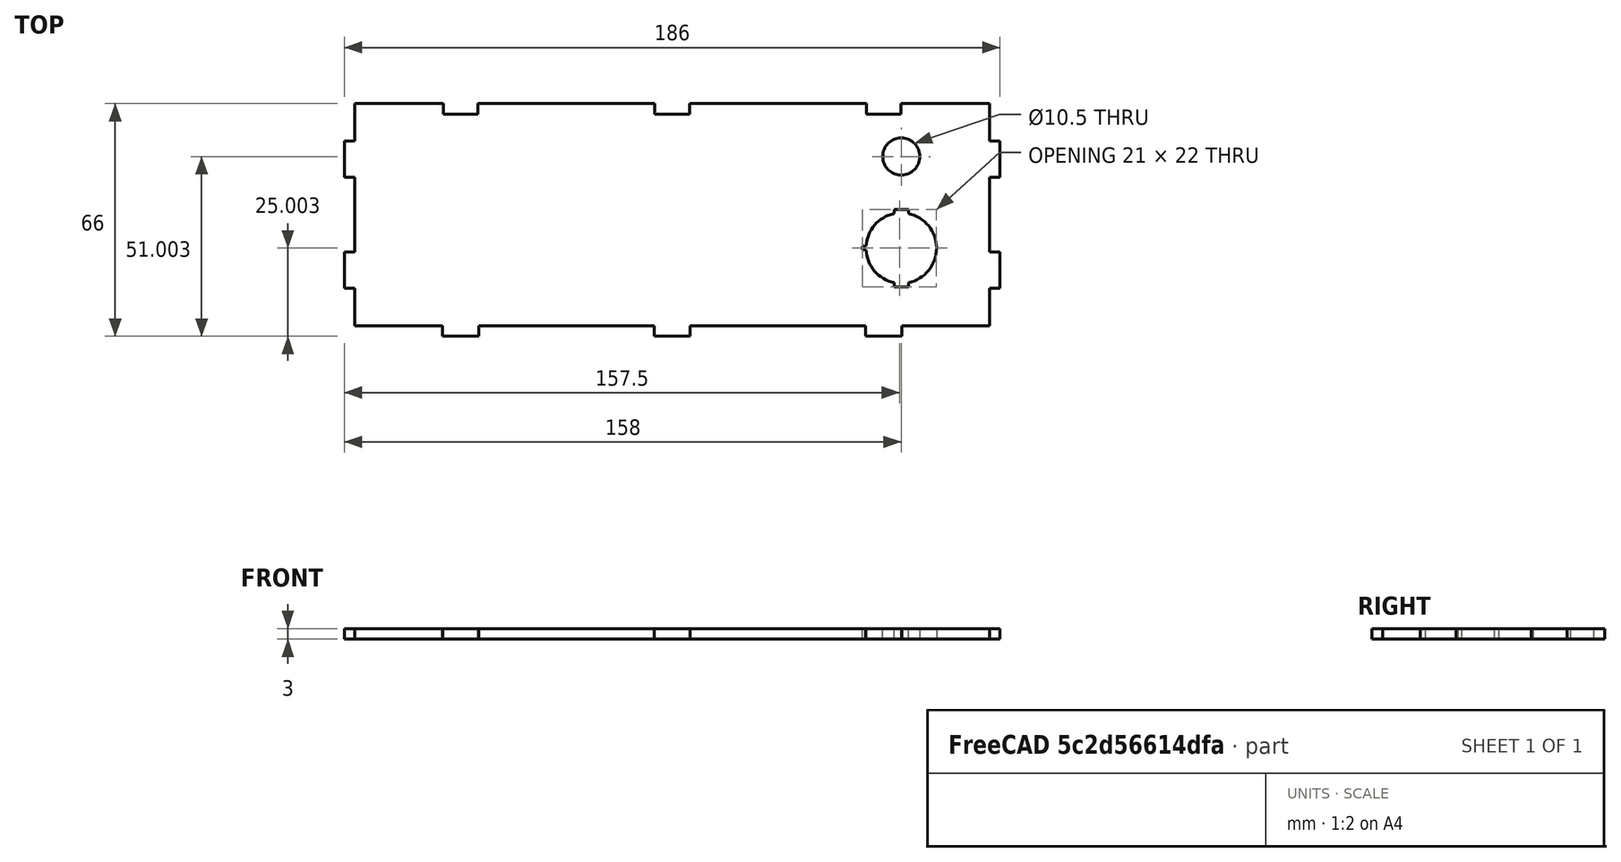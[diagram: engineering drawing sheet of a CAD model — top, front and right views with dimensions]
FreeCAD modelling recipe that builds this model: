
FCSTD DOCUMENT  (FreeCAD 0.21R33771 (Git))
Label: point-controller-box-v0.5.5-expand-updated
License: All rights reserved
LicenseURL: http://en.wikipedia.org/wiki/All_rights_reserved
objects: Part::Feature×7, Part::Part2DObjectPython×7, Sketcher::SketchObject×6, Part::Mirroring×1
note: 21 computed .brp shape members not serialized (recipe doc carries the construction recipe); baked Part::Feature solids carry a one-line shape summary decoded from their .brp

FEATURE [Part::Feature] test
  Placement = pos=(93,51,93) rot=(1,0,0;1.5708rad)
  shape: bbox 186 x 51 x 3 mm, 46 faces (baked)
FEATURE [Part::Feature] test001
  Placement = pos=(196,63,-60) rot=(0,1,0;1.5708rad)
  shape: bbox 63.37 x 126 x 3 mm, 38 faces (baked)
FEATURE [Part::Feature] test002
  Placement = pos=(93,206.207,88.2734) rot=(0.121054,0,0;3.02024rad)
  shape: bbox 186 x 126.9 x 3 mm, 56 faces (baked)
FEATURE [Part::Feature] test003
  Placement = pos=(196,199,123) rot=(0,1,0;1.5708rad)
  shape: bbox 63.37 x 126 x 3 mm, 38 faces (baked)
FEATURE [Part::Feature] test004
  Placement = pos=(93,338.933,-30) rot=(1,0,0;1.5708rad)
  shape: bbox 186 x 66 x 3 mm, 46 faces (baked)
FEATURE [Part::Feature] test005
  Placement = pos=(289,335.933,33) rot=(0,1,0;3.14159rad)
  shape: bbox 186 x 126 x 3 mm, 46 faces (baked)
FEATURE [Part::Feature] test006
  Placement = pos=(93,474.933,-30) rot=(1,0,0;1.5708rad)
  shape: bbox 186 x 66 x 3 mm, 59 faces (baked)
FEATURE [Part::Part2DObjectPython] Shape2DView  label="Shape2DView-Front"  # Draft 2D object (typed FeaturePython)
  AutoUpdate = true
  Base = -> test
  Clip = false
  FuseArch = false
  HiddenLines = false
  InPlace = true
  OnlySolids = false
  Projection = (0,0,1)
  ProjectionMode = 0
  SegmentLength = 0.05
  Tessellation = false
  VisibleOnly = false
FEATURE [Part::Part2DObjectPython] Shape2DView001  # Draft 2D object (typed FeaturePython)
  AutoUpdate = true
  Base = -> test001
  Clip = false
  FuseArch = false
  HiddenLines = false
  InPlace = true
  OnlySolids = false
  Projection = (0,0,1)
  ProjectionMode = 0
  SegmentLength = 0.05
  Tessellation = false
  VisibleOnly = false
FEATURE [Part::Part2DObjectPython] Shape2DView002  # Draft 2D object (typed FeaturePython)
  AutoUpdate = true
  Base = -> test002
  Clip = false
  FuseArch = false
  HiddenLines = false
  InPlace = true
  OnlySolids = false
  Projection = (0,0,1)
  ProjectionMode = 0
  SegmentLength = 0.05
  Tessellation = false
  VisibleOnly = false
FEATURE [Part::Part2DObjectPython] Shape2DView003  # Draft 2D object (typed FeaturePython)
  AutoUpdate = true
  Base = -> test003
  Clip = false
  FuseArch = false
  HiddenLines = false
  InPlace = true
  OnlySolids = false
  Projection = (0,0,1)
  ProjectionMode = 0
  SegmentLength = 0.05
  Tessellation = false
  VisibleOnly = false
FEATURE [Part::Part2DObjectPython] Shape2DView004  # Draft 2D object (typed FeaturePython)
  AutoUpdate = true
  Base = -> test004
  Clip = false
  FuseArch = false
  HiddenLines = false
  InPlace = true
  OnlySolids = false
  Projection = (0,0,1)
  ProjectionMode = 0
  SegmentLength = 0.05
  Tessellation = false
  VisibleOnly = false
FEATURE [Part::Part2DObjectPython] Shape2DView005  # Draft 2D object (typed FeaturePython)
  AutoUpdate = true
  Base = -> test005
  Clip = false
  FuseArch = false
  HiddenLines = false
  InPlace = true
  OnlySolids = false
  Projection = (0,0,1)
  ProjectionMode = 0
  SegmentLength = 0.05
  Tessellation = false
  VisibleOnly = false
FEATURE [Part::Part2DObjectPython] Shape2DView006  # Draft 2D object (typed FeaturePython)
  AutoUpdate = true
  Base = -> test006
  Clip = false
  FuseArch = false
  HiddenLines = false
  InPlace = true
  OnlySolids = false
  Projection = (0,0,1)
  ProjectionMode = 0
  SegmentLength = 0.05
  Tessellation = false
  VisibleOnly = false
FEATURE [Sketcher::SketchObject] Sketch  label="Sketch-Front"
  FullyConstrained = false
  sketch-geometry (44):
    g0: LineSegment StartX=3 StartY=51 StartZ=0 EndX=28.1 EndY=51 EndZ=0
    g1: LineSegment StartX=28.1 StartY=51 StartZ=0 EndX=28.1 EndY=47.95 EndZ=0
    g2: LineSegment StartX=3 StartY=44.1 StartZ=0 EndX=3 EndY=51 EndZ=0
    g3: LineSegment StartX=28.1 StartY=47.95 StartZ=0 EndX=37.9 EndY=47.95 EndZ=0
    g4: LineSegment StartX=37.9 StartY=51 StartZ=0 EndX=37.9 EndY=47.95 EndZ=0
    g5: LineSegment StartX=37.9 StartY=51 StartZ=0 EndX=88.1 EndY=51 EndZ=0
    g6: LineSegment StartX=88.1 StartY=51 StartZ=0 EndX=88.1 EndY=47.95 EndZ=0
    g7: LineSegment StartX=88.1 StartY=47.95 StartZ=0 EndX=97.9 EndY=47.95 EndZ=0
    g8: LineSegment StartX=97.9 StartY=51 StartZ=0 EndX=97.9 EndY=47.95 EndZ=0
    g9: LineSegment StartX=97.9 StartY=51 StartZ=0 EndX=148.1 EndY=51 EndZ=0
    g10: LineSegment StartX=148.1 StartY=51 StartZ=0 EndX=148.1 EndY=47.95 EndZ=0
    g11: LineSegment StartX=148.1 StartY=47.95 StartZ=0 EndX=157.9 EndY=47.95 EndZ=0
    g12: LineSegment StartX=157.9 StartY=51 StartZ=0 EndX=157.9 EndY=47.95 EndZ=0
    g13: LineSegment StartX=157.9 StartY=51 StartZ=0 EndX=183 EndY=51 EndZ=0
    g14: LineSegment StartX=183 StartY=51 StartZ=0 EndX=183 EndY=44.1 EndZ=0
    g15: LineSegment StartX=3 StartY=44.1 StartZ=0 EndX=0 EndY=44.1 EndZ=0
    g16: LineSegment StartX=183 StartY=44.1 StartZ=0 EndX=186 EndY=44.1 EndZ=0
    g17: LineSegment StartX=186 StartY=33.9 StartZ=0 EndX=186 EndY=44.1 EndZ=0
    g18: LineSegment StartX=183 StartY=33.9 StartZ=0 EndX=186 EndY=33.9 EndZ=0
    g19: LineSegment StartX=183 StartY=33.9 StartZ=0 EndX=183 EndY=20.1 EndZ=0
    g20: LineSegment StartX=183 StartY=20.1 StartZ=0 EndX=186 EndY=20.1 EndZ=0
    g21: LineSegment StartX=186 StartY=9.9 StartZ=0 EndX=186 EndY=20.1 EndZ=0
    g22: LineSegment StartX=183 StartY=9.9 StartZ=0 EndX=186 EndY=9.9 EndZ=0
    g23: LineSegment StartX=183 StartY=9.9 StartZ=0 EndX=183 EndY=3 EndZ=0
    g24: LineSegment StartX=183 StartY=3 StartZ=0 EndX=158.1 EndY=3 EndZ=0
    g25: LineSegment StartX=158.1 StartY=3 StartZ=0 EndX=158.1 EndY=1.69e-14 EndZ=0
    g26: LineSegment StartX=147.9 StartY=1.6e-14 StartZ=0 EndX=158.1 EndY=1.6e-14 EndZ=0
    g27: LineSegment StartX=147.9 StartY=3 StartZ=0 EndX=147.9 EndY=1.69e-14 EndZ=0
    g28: LineSegment StartX=147.9 StartY=3 StartZ=0 EndX=98.1 EndY=3 EndZ=0
    g29: LineSegment StartX=98.1 StartY=3 StartZ=0 EndX=98.1 EndY=7.1e-15 EndZ=0
    g30: LineSegment StartX=87.9 StartY=6.2e-15 StartZ=0 EndX=98.1 EndY=6.2e-15 EndZ=0
    g31: LineSegment StartX=87.9 StartY=3 StartZ=0 EndX=87.9 EndY=7.1e-15 EndZ=0
    g32: LineSegment StartX=87.9 StartY=3 StartZ=0 EndX=38.1 EndY=3 EndZ=0
    g33: LineSegment StartX=38.1 StartY=3 StartZ=0 EndX=38.1 EndY=-2.7e-15 EndZ=0
    g34: LineSegment StartX=27.9 StartY=-3.6e-15 StartZ=0 EndX=38.1 EndY=-3.6e-15 EndZ=0
    g35: LineSegment StartX=27.9 StartY=3 StartZ=0 EndX=27.9 EndY=-2.7e-15 EndZ=0
    g36: LineSegment StartX=27.9 StartY=3 StartZ=0 EndX=3 EndY=3 EndZ=0
    g37: LineSegment StartX=3 StartY=3 StartZ=0 EndX=3 EndY=9.9 EndZ=0
    g38: LineSegment StartX=3 StartY=9.9 StartZ=0 EndX=0 EndY=9.9 EndZ=0
    g39: LineSegment StartX=0 StartY=20.1 StartZ=0 EndX=0 EndY=9.9 EndZ=0
    g40: LineSegment StartX=3 StartY=20.1 StartZ=0 EndX=0 EndY=20.1 EndZ=0
    g41: LineSegment StartX=3 StartY=20.1 StartZ=0 EndX=3 EndY=33.9 EndZ=0
    g42: LineSegment StartX=3 StartY=33.9 StartZ=0 EndX=0 EndY=33.9 EndZ=0
    g43: LineSegment StartX=0 StartY=44.1 StartZ=0 EndX=0 EndY=33.9 EndZ=0
FEATURE [Part::Mirroring] Mirror  label="Shape2DView003 (mirrored)"
  Base = (309.469,126.906,35.2508)
  Normal = (0.997697,-0.0191098,0.0650815)
  Source = -> Shape2DView003
FEATURE [Sketcher::SketchObject] Sketch001  label="Sketch-Right"
  FullyConstrained = false
  Placement = pos=(5.21681,-0.0999223,-39.8313) rot=(-0.01915,-0.999817,0;0.130255rad)
  sketch-geometry (37):
    g0: LineSegment StartX=366.687 StartY=259.944 StartZ=0 EndX=377.895 EndY=259.515 EndZ=0
    g1: LineSegment StartX=377.778 StartY=256.467 StartZ=0 EndX=377.895 EndY=259.515 EndZ=0
    g2: LineSegment StartX=377.778 StartY=256.467 StartZ=0 EndX=387.571 EndY=256.092 EndZ=0
    g3: LineSegment StartX=387.571 StartY=256.092 StartZ=0 EndX=387.687 EndY=259.14 EndZ=0
    g4: LineSegment StartX=387.687 StartY=259.14 StartZ=0 EndX=409.371 EndY=258.309 EndZ=0
    g5: LineSegment StartX=409.255 StartY=255.261 StartZ=0 EndX=409.371 EndY=258.309 EndZ=0
    g6: LineSegment StartX=409.255 StartY=255.261 StartZ=0 EndX=419.047 EndY=254.886 EndZ=0
    g7: LineSegment StartX=419.047 StartY=254.886 StartZ=0 EndX=419.164 EndY=257.933 EndZ=0
    g8: LineSegment StartX=419.164 StartY=257.933 StartZ=0 EndX=430.006 EndY=257.518 EndZ=0
    g9: LineSegment StartX=430.006 StartY=257.518 StartZ=0 EndX=428.93 EndY=229.438 EndZ=0
    g10: LineSegment StartX=428.93 StartY=229.438 StartZ=0 EndX=425.882 EndY=229.555 EndZ=0
    g11: LineSegment StartX=425.507 StartY=219.762 StartZ=0 EndX=425.882 EndY=229.555 EndZ=0
    g12: LineSegment StartX=428.555 StartY=219.646 StartZ=0 EndX=425.507 EndY=219.762 EndZ=0
    g13: LineSegment StartX=428.555 StartY=219.646 StartZ=0 EndX=426.633 EndY=169.482 EndZ=0
    g14: LineSegment StartX=426.633 StartY=169.482 StartZ=0 EndX=423.585 EndY=169.599 EndZ=0
    g15: LineSegment StartX=423.21 StartY=159.806 StartZ=0 EndX=423.585 EndY=169.599 EndZ=0
    g16: LineSegment StartX=426.257 StartY=159.69 StartZ=0 EndX=423.21 EndY=159.806 EndZ=0
    g17: LineSegment StartX=425.181 StartY=131.61 StartZ=0 EndX=418.087 EndY=131.882 EndZ=0
    g18: LineSegment StartX=418.087 StartY=131.882 StartZ=0 EndX=418.203 EndY=134.93 EndZ=0
    g19: LineSegment StartX=426.257 StartY=159.69 StartZ=0 EndX=425.181 EndY=131.61 EndZ=0
    g20: LineSegment StartX=408.41 StartY=135.305 StartZ=0 EndX=418.203 EndY=134.93 EndZ=0
    g21: LineSegment StartX=408.294 StartY=132.257 StartZ=0 EndX=408.41 EndY=135.305 EndZ=0
    g22: LineSegment StartX=408.294 StartY=132.257 StartZ=0 EndX=394.104 EndY=132.801 EndZ=0
    g23: LineSegment StartX=394.104 StartY=132.801 StartZ=0 EndX=394.221 EndY=135.849 EndZ=0
    g24: LineSegment StartX=384.428 StartY=136.224 StartZ=0 EndX=394.221 EndY=135.849 EndZ=0
    g25: LineSegment StartX=384.311 StartY=133.176 StartZ=0 EndX=384.428 EndY=136.224 EndZ=0
    g26: LineSegment StartX=384.311 StartY=133.176 StartZ=0 EndX=377.216 EndY=133.448 EndZ=0
    g27: LineSegment StartX=377.216 StartY=133.448 StartZ=0 EndX=375.07 EndY=159.237 EndZ=0
    g28: LineSegment StartX=375.07 StartY=159.237 StartZ=0 EndX=372.08 EndY=158.988 EndZ=0
    g29: LineSegment StartX=371.234 StartY=169.153 StartZ=0 EndX=372.08 EndY=158.988 EndZ=0
    g30: LineSegment StartX=374.224 StartY=169.402 StartZ=0 EndX=371.234 EndY=169.153 EndZ=0
    g31: LineSegment StartX=374.224 StartY=169.402 StartZ=0 EndX=369.93 EndY=220.979 EndZ=0
    g32: LineSegment StartX=369.93 StartY=220.979 StartZ=0 EndX=366.941 EndY=220.73 EndZ=0
    g33: LineSegment StartX=366.095 StartY=230.895 StartZ=0 EndX=366.941 EndY=220.73 EndZ=0
    g34: LineSegment StartX=369.084 StartY=231.144 StartZ=0 EndX=366.095 EndY=230.895 EndZ=0
    g35: LineSegment StartX=369.084 StartY=231.144 StartZ=0 EndX=366.938 EndY=256.933 EndZ=0
    g36: LineSegment StartX=366.938 StartY=256.933 StartZ=0 EndX=366.687 EndY=259.944 EndZ=0
FEATURE [Sketcher::SketchObject] Sketch002  label="Sketch-Left"
  FullyConstrained = false
  sketch-geometry (37):
    g0: LineSegment StartX=259.366 StartY=126 StartZ=0 EndX=248.15 EndY=126 EndZ=0
    g1: LineSegment StartX=248.15 StartY=122.95 StartZ=0 EndX=248.15 EndY=126 EndZ=0
    g2: LineSegment StartX=238.35 StartY=122.95 StartZ=0 EndX=248.15 EndY=122.95 EndZ=0
    g3: LineSegment StartX=238.35 StartY=122.95 StartZ=0 EndX=238.35 EndY=126 EndZ=0
    g4: LineSegment StartX=238.35 StartY=126 StartZ=0 EndX=216.65 EndY=126 EndZ=0
    g5: LineSegment StartX=216.65 StartY=122.95 StartZ=0 EndX=216.65 EndY=126 EndZ=0
    g6: LineSegment StartX=206.85 StartY=122.95 StartZ=0 EndX=216.65 EndY=122.95 EndZ=0
    g7: LineSegment StartX=206.85 StartY=122.95 StartZ=0 EndX=206.85 EndY=126 EndZ=0
    g8: LineSegment StartX=206.85 StartY=126 StartZ=0 EndX=196 EndY=126 EndZ=0
    g9: LineSegment StartX=196 StartY=126 StartZ=0 EndX=196 EndY=97.9 EndZ=0
    g10: LineSegment StartX=196 StartY=97.9 StartZ=0 EndX=199.05 EndY=97.9 EndZ=0
    g11: LineSegment StartX=199.05 StartY=97.9 StartZ=0 EndX=199.05 EndY=88.1 EndZ=0
    g12: LineSegment StartX=196 StartY=88.1 StartZ=0 EndX=199.05 EndY=88.1 EndZ=0
    g13: LineSegment StartX=196 StartY=88.1 StartZ=0 EndX=196 EndY=37.9 EndZ=0
    g14: LineSegment StartX=196 StartY=37.9 StartZ=0 EndX=199.05 EndY=37.9 EndZ=0
    g15: LineSegment StartX=199.05 StartY=37.9 StartZ=0 EndX=199.05 EndY=28.1 EndZ=0
    g16: LineSegment StartX=196 StartY=28.1 StartZ=0 EndX=199.05 EndY=28.1 EndZ=0
    g17: LineSegment StartX=196 StartY=7.1e-15 StartZ=0 EndX=203.1 EndY=6.1e-15 EndZ=0
    g18: LineSegment StartX=203.1 StartY=9.5e-15 StartZ=0 EndX=203.1 EndY=3.05 EndZ=0
    g19: LineSegment StartX=196 StartY=28.1 StartZ=0 EndX=196 EndY=0 EndZ=0
    g20: LineSegment StartX=203.1 StartY=3.05 StartZ=0 EndX=212.9 EndY=3.05 EndZ=0
    g21: LineSegment StartX=212.9 StartY=7.3e-15 StartZ=0 EndX=212.9 EndY=3.05 EndZ=0
    g22: LineSegment StartX=212.9 StartY=4.6e-15 StartZ=0 EndX=227.1 EndY=2.5e-15 EndZ=0
    g23: LineSegment StartX=227.1 StartY=-2.9e-15 StartZ=0 EndX=227.1 EndY=3.05 EndZ=0
    g24: LineSegment StartX=227.1 StartY=3.05 StartZ=0 EndX=236.9 EndY=3.05 EndZ=0
    g25: LineSegment StartX=236.9 StartY=-5.1e-15 StartZ=0 EndX=236.9 EndY=3.05 EndZ=0
    g26: LineSegment StartX=236.9 StartY=1.1e-15 StartZ=0 EndX=244 EndY=0 EndZ=0
    g27: LineSegment StartX=244 StartY=0 StartZ=0 EndX=247.133 EndY=25.6875 EndZ=0
    g28: LineSegment StartX=247.133 StartY=25.6875 StartZ=0 EndX=250.111 EndY=25.3243 EndZ=0
    g29: LineSegment StartX=251.345 StartY=35.4493 StartZ=0 EndX=250.111 EndY=25.3243 EndZ=0
    g30: LineSegment StartX=248.367 StartY=35.8125 StartZ=0 EndX=251.345 EndY=35.4493 EndZ=0
    g31: LineSegment StartX=248.367 StartY=35.8125 StartZ=0 EndX=254.633 EndY=87.1875 EndZ=0
    g32: LineSegment StartX=254.633 StartY=87.1875 StartZ=0 EndX=257.611 EndY=86.8243 EndZ=0
    g33: LineSegment StartX=258.845 StartY=96.9493 StartZ=0 EndX=257.611 EndY=86.8243 EndZ=0
    g34: LineSegment StartX=255.867 StartY=97.3125 StartZ=0 EndX=258.845 EndY=96.9493 EndZ=0
    g35: LineSegment StartX=255.867 StartY=97.3125 StartZ=0 EndX=259 EndY=123 EndZ=0
    g36: LineSegment StartX=259 StartY=123 StartZ=0 EndX=259.366 EndY=126 EndZ=0
FEATURE [Sketcher::SketchObject] Sketch003  label="Sketch-Top"
  FullyConstrained = false
  sketch-geometry (68):
    g0: LineSegment StartX=0 StartY=262.933 StartZ=0 EndX=28.1 EndY=262.933 EndZ=0
    g1: LineSegment StartX=37.9 StartY=262.933 StartZ=0 EndX=88.1 EndY=262.933 EndZ=0
    g2: LineSegment StartX=97.9 StartY=262.933 StartZ=0 EndX=148.1 EndY=262.933 EndZ=0
    g3: LineSegment StartX=157.9 StartY=262.933 StartZ=0 EndX=186 EndY=262.93 EndZ=0
    g4: LineSegment StartX=0 StartY=236.856 StartZ=0 EndX=0 EndY=262.933 EndZ=0
    g5: LineSegment StartX=5.1e-15 StartY=236.856 StartZ=0 EndX=3.05 EndY=236.856 EndZ=0
    g6: LineSegment StartX=3.05 StartY=227.056 StartZ=0 EndX=3.05 EndY=236.856 EndZ=0
    g7: LineSegment StartX=5.1e-15 StartY=227.056 StartZ=0 EndX=3.05 EndY=227.056 EndZ=0
    g8: LineSegment StartX=0 StartY=174.9 StartZ=0 EndX=0 EndY=227.056 EndZ=0
    g9: LineSegment StartX=5.6e-15 StartY=174.9 StartZ=0 EndX=3.05 EndY=174.9 EndZ=0
    g10: LineSegment StartX=3.05 StartY=165.1 StartZ=0 EndX=3.05 EndY=174.9 EndZ=0
    g11: LineSegment StartX=5.6e-15 StartY=165.1 StartZ=0 EndX=3.05 EndY=165.1 EndZ=0
    g12: LineSegment StartX=0 StartY=136 StartZ=0 EndX=0 EndY=165.1 EndZ=0
    g13: LineSegment StartX=28.1 StartY=136 StartZ=0 EndX=0 EndY=136 EndZ=0
    g14: LineSegment StartX=28.1 StartY=139.022 StartZ=0 EndX=28.1 EndY=136 EndZ=0
    g15: LineSegment StartX=37.9 StartY=139.022 StartZ=0 EndX=28.1 EndY=139.022 EndZ=0
    g16: LineSegment StartX=37.9 StartY=139.022 StartZ=0 EndX=37.9 EndY=136 EndZ=0
    g17: LineSegment StartX=88.1 StartY=136 StartZ=0 EndX=37.9 EndY=136 EndZ=0
    g18: LineSegment StartX=88.1 StartY=139.022 StartZ=0 EndX=88.1 EndY=136 EndZ=0
    g19: LineSegment StartX=97.9 StartY=139.022 StartZ=0 EndX=88.1 EndY=139.022 EndZ=0
    g20: LineSegment StartX=97.9 StartY=139.022 StartZ=0 EndX=97.9 EndY=136 EndZ=0
    g21: LineSegment StartX=148.1 StartY=136 StartZ=0 EndX=97.9 EndY=136 EndZ=0
    g22: LineSegment StartX=148.1 StartY=139.022 StartZ=0 EndX=148.1 EndY=136 EndZ=0
    g23: LineSegment StartX=157.9 StartY=139.022 StartZ=0 EndX=148.1 EndY=139.022 EndZ=0
    g24: LineSegment StartX=157.9 StartY=139.022 StartZ=0 EndX=157.9 EndY=136 EndZ=0
    g25: LineSegment StartX=186 StartY=136 StartZ=0 EndX=157.9 EndY=136 EndZ=0
    g26: LineSegment StartX=186 StartY=165.1 StartZ=0 EndX=186 EndY=136 EndZ=0
    g27: LineSegment StartX=183.241 StartY=165.1 StartZ=0 EndX=186 EndY=165.1 EndZ=0
    g28: ArcOfCircle CenterX=183.057 CenterY=165.207 CenterZ=0 NormalX=0 NormalY=0 NormalZ=1 AngleXU=0 Radius=0.213333 StartAngle=2.0944 EndAngle=5.75959
    g29: LineSegment StartX=182.95 StartY=165.391 StartZ=0 EndX=182.95 EndY=174.609 EndZ=0
    g30: ArcOfCircle CenterX=183.057 CenterY=174.793 CenterZ=0 NormalX=0 NormalY=0 NormalZ=1 AngleXU=0 Radius=0.213333 StartAngle=0.523599 EndAngle=4.18879
    g31: LineSegment StartX=183.241 StartY=174.9 StartZ=0 EndX=186 EndY=174.9 EndZ=0
    g32: LineSegment StartX=186 StartY=227.056 StartZ=0 EndX=186 EndY=174.9 EndZ=0
    g33: LineSegment StartX=183.241 StartY=227.056 StartZ=0 EndX=186 EndY=227.056 EndZ=0
    g34: ArcOfCircle CenterX=183.057 CenterY=227.162 CenterZ=0 NormalX=0 NormalY=0 NormalZ=1 AngleXU=0 Radius=0.213333 StartAngle=2.0944 EndAngle=5.75959
    g35: LineSegment StartX=182.95 StartY=227.347 StartZ=0 EndX=182.95 EndY=236.564 EndZ=0
    g36: ArcOfCircle CenterX=183.057 CenterY=236.749 CenterZ=0 NormalX=0 NormalY=0 NormalZ=1 AngleXU=0 Radius=0.213333 StartAngle=0.523599 EndAngle=4.18879
    g37: LineSegment StartX=183.241 StartY=236.856 StartZ=0 EndX=186 EndY=236.856 EndZ=0
    g38: LineSegment StartX=186 StartY=262.933 StartZ=0 EndX=186 EndY=236.856 EndZ=0
    g39: LineSegment StartX=157.9 StartY=262.933 StartZ=0 EndX=157.9 EndY=259.861 EndZ=0
    g40: LineSegment StartX=157.9 StartY=259.861 StartZ=0 EndX=148.1 EndY=259.861 EndZ=0
    g41: LineSegment StartX=148.1 StartY=262.933 StartZ=0 EndX=148.1 EndY=259.861 EndZ=0
    g42: LineSegment StartX=97.9 StartY=262.933 StartZ=0 EndX=97.9 EndY=259.861 EndZ=0
    g43: LineSegment StartX=97.9 StartY=259.861 StartZ=0 EndX=88.1 EndY=259.861 EndZ=0
    g44: LineSegment StartX=88.1 StartY=262.933 StartZ=0 EndX=88.1 EndY=259.861 EndZ=0
    g45: LineSegment StartX=37.9 StartY=262.933 StartZ=0 EndX=37.9 EndY=259.861 EndZ=0
    g46: LineSegment StartX=37.9 StartY=259.861 StartZ=0 EndX=28.1 EndY=259.861 EndZ=0
    g47: LineSegment StartX=28.1 StartY=262.933 StartZ=0 EndX=28.1 EndY=259.861 EndZ=0
    g48: LineSegment StartX=28.1 StartY=262.62 StartZ=0 EndX=28.1 EndY=259.861 EndZ=0
    g49: LineSegment StartX=37.9 StartY=262.62 StartZ=0 EndX=37.9 EndY=259.861 EndZ=0
    g50: LineSegment StartX=88.1 StartY=262.62 StartZ=0 EndX=88.1 EndY=259.861 EndZ=0
    g51: LineSegment StartX=97.9 StartY=262.62 StartZ=0 EndX=97.9 EndY=259.861 EndZ=0
    g52: LineSegment StartX=148.1 StartY=262.62 StartZ=0 EndX=148.1 EndY=259.861 EndZ=0
    g53: LineSegment StartX=157.9 StartY=262.62 StartZ=0 EndX=157.9 EndY=259.861 EndZ=0
    g54: LineSegment StartX=28.1 StartY=139.022 StartZ=0 EndX=28.1 EndY=138.709 EndZ=0
    g55: LineSegment StartX=37.9 StartY=139.022 StartZ=0 EndX=37.9 EndY=138.709 EndZ=0
    g56: LineSegment StartX=88.1 StartY=139.022 StartZ=0 EndX=88.1 EndY=138.709 EndZ=0
    g57: LineSegment StartX=97.9 StartY=139.022 StartZ=0 EndX=97.9 EndY=138.709 EndZ=0
    g58: LineSegment StartX=148.1 StartY=139.022 StartZ=0 EndX=148.1 EndY=138.709 EndZ=0
    g59: LineSegment StartX=157.9 StartY=139.022 StartZ=0 EndX=157.9 EndY=138.709 EndZ=0
    g60: LineSegment StartX=79 StartY=207.5 StartZ=0 EndX=107 EndY=207.5 EndZ=0
    g61: LineSegment StartX=107 StartY=207.5 StartZ=0 EndX=107 EndY=191.5 EndZ=0
    g62: LineSegment StartX=107 StartY=191.5 StartZ=0 EndX=79 EndY=191.5 EndZ=0
    g63: LineSegment StartX=79 StartY=191.5 StartZ=0 EndX=79 EndY=207.5 EndZ=0
    g64: Circle CenterX=104.75 CenterY=209.5 CenterZ=0 NormalX=0 NormalY=0 NormalZ=1 AngleXU=0 Radius=1.15
    g65: Circle CenterX=81.25 CenterY=209.5 CenterZ=0 NormalX=0 NormalY=0 NormalZ=1 AngleXU=0 Radius=1.15
    g66: Circle CenterX=104.75 CenterY=185.5 CenterZ=0 NormalX=0 NormalY=0 NormalZ=1 AngleXU=0 Radius=1.15
    g67: Circle CenterX=81.25 CenterY=185.5 CenterZ=0 NormalX=0 NormalY=0 NormalZ=1 AngleXU=0 Radius=1.15
  constraints (28):
    c: DistanceY(g12) = 136
    c: DistanceX(g12) = 0
    c: DistanceY(g3) = 262.93
    c: DistanceX(g3) = 186
    c: Coincident(g60,g61)
    c: Coincident(g61,g62)
    c: Coincident(g62,g63)
    c: Coincident(g63,g60)
    c: Horizontal(g60)
    c: Horizontal(g62)
    c: Vertical(g61)
    c: Vertical(g63)
    c: DistanceX(g60,g60) = 28
    c: DistanceY(g61,g61) = 16
    c: DistanceX(g12,g62) = 79
    c: DistanceY(g12,g62) = 55.5
    c: DistanceX(g67,g66) = 23.5
    c: Vertical(g66,g64)
    c: Vertical(g65,g67)
    c: Horizontal(g65,g64)
    c: Horizontal(g67,g66)
    c: Equal(g66,g67)
    c: Equal(g66,g65)
    c: Equal(g66,g64)
    c: Diameter(g66) = 2.3
    c: DistanceX(g62,g67) = 2.25
    c: DistanceY(g66,g64) = 24
    c: DistanceY(g67,g62) = 6
FEATURE [Sketcher::SketchObject] Sketch004  label="Sketch-Base"
  FullyConstrained = false
  sketch-geometry (52):
    g0: LineSegment StartX=379 StartY=395.933 StartZ=0 EndX=354.1 EndY=395.933 EndZ=0
    g1: LineSegment StartX=354.1 StartY=395.933 StartZ=0 EndX=354.1 EndY=398.933 EndZ=0
    g2: LineSegment StartX=379 StartY=371.033 StartZ=0 EndX=379 EndY=395.933 EndZ=0
    g3: LineSegment StartX=343.9 StartY=398.933 StartZ=0 EndX=354.1 EndY=398.933 EndZ=0
    g4: LineSegment StartX=379 StartY=371.033 StartZ=0 EndX=382 EndY=371.033 EndZ=0
    g5: LineSegment StartX=343.9 StartY=395.933 StartZ=0 EndX=343.9 EndY=398.933 EndZ=0
    g6: LineSegment StartX=343.9 StartY=395.933 StartZ=0 EndX=294.1 EndY=395.933 EndZ=0
    g7: LineSegment StartX=294.1 StartY=395.933 StartZ=0 EndX=294.1 EndY=398.933 EndZ=0
    g8: LineSegment StartX=283.9 StartY=398.933 StartZ=0 EndX=294.1 EndY=398.933 EndZ=0
    g9: LineSegment StartX=283.9 StartY=395.933 StartZ=0 EndX=283.9 EndY=398.933 EndZ=0
    g10: LineSegment StartX=283.9 StartY=395.933 StartZ=0 EndX=234.1 EndY=395.933 EndZ=0
    g11: LineSegment StartX=234.1 StartY=395.933 StartZ=0 EndX=234.1 EndY=398.933 EndZ=0
    g12: LineSegment StartX=223.9 StartY=398.933 StartZ=0 EndX=234.1 EndY=398.933 EndZ=0
    g13: LineSegment StartX=223.9 StartY=395.933 StartZ=0 EndX=223.9 EndY=398.933 EndZ=0
    g14: LineSegment StartX=223.9 StartY=395.933 StartZ=0 EndX=199 EndY=395.93 EndZ=0
    g15: LineSegment StartX=199 StartY=395.93 StartZ=0 EndX=199 EndY=371.033 EndZ=0
    g16: LineSegment StartX=199 StartY=371.033 StartZ=0 EndX=196 EndY=371.033 EndZ=0
    g17: LineSegment StartX=196 StartY=360.833 StartZ=0 EndX=196 EndY=371.033 EndZ=0
    g18: LineSegment StartX=199 StartY=360.833 StartZ=0 EndX=196 EndY=360.833 EndZ=0
    g19: LineSegment StartX=199 StartY=360.833 StartZ=0 EndX=199 EndY=311.033 EndZ=0
    g20: LineSegment StartX=199 StartY=311.033 StartZ=0 EndX=196 EndY=311.033 EndZ=0
    g21: LineSegment StartX=196 StartY=300.833 StartZ=0 EndX=196 EndY=311.033 EndZ=0
    g22: LineSegment StartX=199 StartY=300.833 StartZ=0 EndX=196 EndY=300.833 EndZ=0
    g23: LineSegment StartX=199 StartY=300.833 StartZ=0 EndX=199 EndY=275.933 EndZ=0
    g24: LineSegment StartX=199 StartY=275.933 StartZ=0 EndX=223.9 EndY=275.933 EndZ=0
    g25: LineSegment StartX=223.9 StartY=275.933 StartZ=0 EndX=223.9 EndY=272.933 EndZ=0
    g26: LineSegment StartX=234.1 StartY=272.933 StartZ=0 EndX=223.9 EndY=272.933 EndZ=0
    g27: LineSegment StartX=234.1 StartY=275.933 StartZ=0 EndX=234.1 EndY=272.933 EndZ=0
    g28: LineSegment StartX=234.1 StartY=275.933 StartZ=0 EndX=283.9 EndY=275.933 EndZ=0
    g29: LineSegment StartX=283.9 StartY=275.933 StartZ=0 EndX=283.9 EndY=272.933 EndZ=0
    g30: LineSegment StartX=294.1 StartY=272.933 StartZ=0 EndX=283.9 EndY=272.933 EndZ=0
    g31: LineSegment StartX=294.1 StartY=275.933 StartZ=0 EndX=294.1 EndY=272.933 EndZ=0
    g32: LineSegment StartX=294.1 StartY=275.933 StartZ=0 EndX=343.9 EndY=275.933 EndZ=0
    g33: LineSegment StartX=343.9 StartY=275.933 StartZ=0 EndX=343.9 EndY=272.933 EndZ=0
    g34: LineSegment StartX=354.1 StartY=272.933 StartZ=0 EndX=343.9 EndY=272.933 EndZ=0
    g35: LineSegment StartX=354.1 StartY=275.933 StartZ=0 EndX=354.1 EndY=272.933 EndZ=0
    g36: LineSegment StartX=354.1 StartY=275.933 StartZ=0 EndX=379 EndY=275.93 EndZ=0
    g37: LineSegment StartX=379 StartY=275.93 StartZ=0 EndX=379 EndY=300.833 EndZ=0
    g38: LineSegment StartX=379 StartY=300.833 StartZ=0 EndX=382 EndY=300.833 EndZ=0
    g39: LineSegment StartX=382 StartY=311.033 StartZ=0 EndX=382 EndY=300.833 EndZ=0
    g40: LineSegment StartX=379 StartY=311.033 StartZ=0 EndX=382 EndY=311.033 EndZ=0
    g41: LineSegment StartX=379 StartY=311.033 StartZ=0 EndX=379 EndY=360.833 EndZ=0
    g42: LineSegment StartX=379 StartY=360.833 StartZ=0 EndX=382 EndY=360.833 EndZ=0
    g43: LineSegment StartX=382 StartY=371.033 StartZ=0 EndX=382 EndY=360.833 EndZ=0
    g44: Circle CenterX=373 CenterY=289.93 CenterZ=0 NormalX=0 NormalY=0 NormalZ=1 AngleXU=0 Radius=1.6
    g45: Circle CenterX=373 CenterY=366.93 CenterZ=0 NormalX=0 NormalY=0 NormalZ=1 AngleXU=0 Radius=1.6
    g46: Circle CenterX=267 CenterY=289.93 CenterZ=0 NormalX=0 NormalY=0 NormalZ=1 AngleXU=0 Radius=1.6
    g47: Circle CenterX=267 CenterY=366.93 CenterZ=0 NormalX=0 NormalY=0 NormalZ=1 AngleXU=0 Radius=1.6
    g48: Circle CenterX=203 CenterY=391.93 CenterZ=0 NormalX=0 NormalY=0 NormalZ=1 AngleXU=0 Radius=1.6
    g49: Circle CenterX=236 CenterY=391.93 CenterZ=0 NormalX=0 NormalY=0 NormalZ=1 AngleXU=0 Radius=1.6
    g50: Circle CenterX=203 CenterY=331.93 CenterZ=0 NormalX=0 NormalY=0 NormalZ=1 AngleXU=0 Radius=1.6
    g51: Circle CenterX=236 CenterY=331.93 CenterZ=0 NormalX=0 NormalY=0 NormalZ=1 AngleXU=0 Radius=1.6
  constraints (30):
    c: Coincident(g37,g36)
    c: DistanceX(g36) = 379
    c: DistanceY(g36) = 275.93
    c: DistanceY(g36,g44) = 14
    c: DistanceX(g44,g36) = 6
    c: Vertical(g45,g44)
    c: Vertical(g46,g47)
    c: Horizontal(g46,g44)
    c: Horizontal(g47,g45)
    c: DistanceX(g46,g44) = 106
    c: DistanceY(g44,g45) = 77
    c: Equal(g46,g47)
    c: Equal(g46,g45)
    c: Equal(g46,g44)
    c: Diameter(g46) = 3.2
    c: Coincident(g15,g14)
    c: DistanceX(g14) = 199
    c: DistanceY(g14) = 395.93
    c: DistanceX(g14,g48) = 4
    c: DistanceY(g48,g14) = 4
    c: Horizontal(g48,g49)
    c: Horizontal(g50,g51)
    c: Vertical(g49,g51)
    c: Vertical(g48,g50)
    c: DistanceX(g48,g49) = 33
    c: DistanceY(g50,g48) = 60
    c: Equal(g50,g51)
    c: Equal(g50,g49)
    c: Equal(g50,g48)
    c: Diameter(g50) = 3.2
FEATURE [Sketcher::SketchObject] Sketch005  label="Sketch-Rear"
  FullyConstrained = false
  sketch-geometry (87):
    g0: LineSegment StartX=3 StartY=474.93 StartZ=0 EndX=28.1 EndY=474.933 EndZ=0
    g1: LineSegment StartX=28.1 StartY=474.933 StartZ=0 EndX=28.1 EndY=471.88 EndZ=0
    g2: LineSegment StartX=3 StartY=464.283 StartZ=0 EndX=3 EndY=474.93 EndZ=0
    g3: LineSegment StartX=37.9 StartY=471.883 StartZ=0 EndX=28.1 EndY=471.883 EndZ=0
    g4: LineSegment StartX=37.9 StartY=474.933 StartZ=0 EndX=37.9 EndY=471.883 EndZ=0
    g5: LineSegment StartX=37.9 StartY=474.933 StartZ=0 EndX=88.1 EndY=474.933 EndZ=0
    g6: LineSegment StartX=88.1 StartY=474.933 StartZ=0 EndX=88.1 EndY=471.883 EndZ=0
    g7: LineSegment StartX=97.9 StartY=471.883 StartZ=0 EndX=88.1 EndY=471.883 EndZ=0
    g8: LineSegment StartX=97.9 StartY=474.933 StartZ=0 EndX=97.9 EndY=471.883 EndZ=0
    g9: LineSegment StartX=97.9 StartY=474.933 StartZ=0 EndX=148.1 EndY=474.933 EndZ=0
    g10: LineSegment StartX=148.1 StartY=474.933 StartZ=0 EndX=148.1 EndY=471.883 EndZ=0
    g11: LineSegment StartX=157.9 StartY=471.883 StartZ=0 EndX=148.1 EndY=471.883 EndZ=0
    g12: LineSegment StartX=157.9 StartY=474.933 StartZ=0 EndX=157.9 EndY=471.883 EndZ=0
    g13: LineSegment StartX=157.9 StartY=474.933 StartZ=0 EndX=183 EndY=474.933 EndZ=0
    g14: LineSegment StartX=183 StartY=474.933 StartZ=0 EndX=183 EndY=464.283 EndZ=0
    g15: LineSegment StartX=3 StartY=464.283 StartZ=0 EndX=0 EndY=464.283 EndZ=0
    g16: LineSegment StartX=0 StartY=464.283 StartZ=0 EndX=0 EndY=454.083 EndZ=0
    g17: LineSegment StartX=3 StartY=432.783 StartZ=0 EndX=3 EndY=454.083 EndZ=0
    g18: LineSegment StartX=3 StartY=454.083 StartZ=0 EndX=0 EndY=454.083 EndZ=0
    g19: LineSegment StartX=3 StartY=432.783 StartZ=0 EndX=0 EndY=432.783 EndZ=0
    g20: LineSegment StartX=0 StartY=432.783 StartZ=0 EndX=0 EndY=422.583 EndZ=0
    g21: LineSegment StartX=3 StartY=411.933 StartZ=0 EndX=3 EndY=422.583 EndZ=0
    g22: LineSegment StartX=27.9 StartY=411.933 StartZ=0 EndX=3 EndY=411.933 EndZ=0
    g23: LineSegment StartX=3 StartY=422.583 StartZ=0 EndX=0 EndY=422.583 EndZ=0
    g24: LineSegment StartX=27.9 StartY=411.933 StartZ=0 EndX=27.9 EndY=408.933 EndZ=0
    g25: LineSegment StartX=27.9 StartY=408.933 StartZ=0 EndX=38.1 EndY=408.933 EndZ=0
    g26: LineSegment StartX=87.9 StartY=411.933 StartZ=0 EndX=38.1 EndY=411.933 EndZ=0
    g27: LineSegment StartX=38.1 StartY=411.933 StartZ=0 EndX=38.1 EndY=408.933 EndZ=0
    g28: LineSegment StartX=87.9 StartY=411.933 StartZ=0 EndX=87.9 EndY=408.933 EndZ=0
    g29: LineSegment StartX=87.9 StartY=408.933 StartZ=0 EndX=98.1 EndY=408.933 EndZ=0
    g30: LineSegment StartX=147.9 StartY=411.933 StartZ=0 EndX=98.1 EndY=411.933 EndZ=0
    g31: LineSegment StartX=98.1 StartY=411.933 StartZ=0 EndX=98.1 EndY=408.933 EndZ=0
    g32: LineSegment StartX=147.9 StartY=411.933 StartZ=0 EndX=147.9 EndY=408.933 EndZ=0
    g33: LineSegment StartX=147.9 StartY=408.933 StartZ=0 EndX=158.1 EndY=408.933 EndZ=0
    g34: LineSegment StartX=183 StartY=411.933 StartZ=0 EndX=158.1 EndY=411.933 EndZ=0
    g35: LineSegment StartX=183 StartY=422.583 StartZ=0 EndX=183 EndY=411.933 EndZ=0
    g36: LineSegment StartX=158.1 StartY=411.933 StartZ=0 EndX=158.1 EndY=408.933 EndZ=0
    g37: LineSegment StartX=183 StartY=422.583 StartZ=0 EndX=186 EndY=422.583 EndZ=0
    g38: LineSegment StartX=183 StartY=464.283 StartZ=0 EndX=186 EndY=464.283 EndZ=0
    g39: LineSegment StartX=186 StartY=422.583 StartZ=0 EndX=186 EndY=432.783 EndZ=0
    g40: LineSegment StartX=183 StartY=454.083 StartZ=0 EndX=183 EndY=432.783 EndZ=0
    g41: LineSegment StartX=183 StartY=432.783 StartZ=0 EndX=186 EndY=432.783 EndZ=0
    g42: LineSegment StartX=186 StartY=454.083 StartZ=0 EndX=186 EndY=464.283 EndZ=0
    g43: LineSegment StartX=183 StartY=454.083 StartZ=0 EndX=186 EndY=454.083 EndZ=0
    g44: LineSegment StartX=160 StartY=443.731 StartZ=0 EndX=160 EndY=444.933 EndZ=0
    g45: ArcOfCircle CenterX=158 CenterY=433.933 CenterZ=0 NormalX=0 NormalY=0 NormalZ=1 AngleXU=3.14159 Radius=10 StartAngle=1.77215 EndAngle=4.51103
    g46: LineSegment StartX=160 StartY=422.933 StartZ=0 EndX=160 EndY=424.136 EndZ=0
    g47: LineSegment StartX=156 StartY=422.933 StartZ=0 EndX=160 EndY=422.933 EndZ=0
    g48: LineSegment StartX=156 StartY=424.136 StartZ=0 EndX=156 EndY=422.933 EndZ=0
    g49: ArcOfCircle CenterX=158 CenterY=433.933 CenterZ=0 NormalX=0 NormalY=0 NormalZ=1 AngleXU=3.14159 Radius=10 StartAngle=0.0500209 EndAngle=1.36944
    g50: LineSegment StartX=147 StartY=433.433 StartZ=0 EndX=148.013 EndY=433.433 EndZ=0
    g51: LineSegment StartX=147 StartY=434.433 StartZ=0 EndX=147 EndY=433.433 EndZ=0
    g52: LineSegment StartX=148.013 StartY=434.433 StartZ=0 EndX=147 EndY=434.433 EndZ=0
    g53: ArcOfCircle CenterX=158 CenterY=433.933 CenterZ=0 NormalX=0 NormalY=0 NormalZ=1 AngleXU=3.14159 Radius=10 StartAngle=4.91375 EndAngle=6.23316
    g54: LineSegment StartX=156 StartY=444.933 StartZ=0 EndX=156 EndY=443.731 EndZ=0
    g55: LineSegment StartX=160 StartY=444.933 StartZ=0 EndX=156 EndY=444.933 EndZ=0
    g56: Circle CenterX=158 CenterY=459.933 CenterZ=0 NormalX=0 NormalY=0 NormalZ=-1 AngleXU=0 Radius=5.5
    g57: GeomPoint X=4 Y=467.88 Z=0
    g58: GeomPoint X=4 Y=453.38 Z=0
    g59: LineSegment StartX=6.5 StartY=453.38 StartZ=0 EndX=20.5 EndY=453.38 EndZ=0
    g60: LineSegment StartX=20.5 StartY=453.38 StartZ=0 EndX=20.5 EndY=467.88 EndZ=0
    g61: LineSegment StartX=20.5 StartY=467.88 StartZ=0 EndX=6.5 EndY=467.88 EndZ=0
    g62: LineSegment StartX=6.5 StartY=467.88 StartZ=0 EndX=6.5 EndY=453.38 EndZ=0
    g63: LineSegment StartX=23 StartY=453.38 StartZ=0 EndX=36.5 EndY=453.38 EndZ=0
    g64: LineSegment StartX=36.5 StartY=453.38 StartZ=0 EndX=36.5 EndY=467.88 EndZ=0
    g65: LineSegment StartX=36.5 StartY=467.88 StartZ=0 EndX=23 EndY=467.88 EndZ=0
    g66: LineSegment StartX=23 StartY=467.88 StartZ=0 EndX=23 EndY=453.38 EndZ=0
    g67: LineSegment StartX=39 StartY=467.88 StartZ=0 EndX=53 EndY=467.88 EndZ=0
    g68: LineSegment StartX=53 StartY=467.88 StartZ=0 EndX=53 EndY=453.38 EndZ=0
    g69: LineSegment StartX=53 StartY=453.38 StartZ=0 EndX=39 EndY=453.38 EndZ=0
    g70: LineSegment StartX=39 StartY=453.38 StartZ=0 EndX=39 EndY=467.88 EndZ=0
    g71: LineSegment StartX=55 StartY=453.38 StartZ=0 EndX=68.5 EndY=453.38 EndZ=0
    g72: LineSegment StartX=68.5 StartY=453.38 StartZ=0 EndX=68.5 EndY=467.88 EndZ=0
    g73: LineSegment StartX=68.5 StartY=467.88 StartZ=0 EndX=55 EndY=467.88 EndZ=0
    g74: LineSegment StartX=55 StartY=467.88 StartZ=0 EndX=55 EndY=453.38 EndZ=0
    g75: LineSegment StartX=76 StartY=453.38 StartZ=0 EndX=93 EndY=453.38 EndZ=0
    g76: LineSegment StartX=93 StartY=453.38 StartZ=0 EndX=93 EndY=467.88 EndZ=0
    g77: LineSegment StartX=93 StartY=467.88 StartZ=0 EndX=76 EndY=467.88 EndZ=0
    g78: LineSegment StartX=76 StartY=467.88 StartZ=0 EndX=76 EndY=453.38 EndZ=0
    g79: LineSegment StartX=95 StartY=453.38 StartZ=0 EndX=104 EndY=453.38 EndZ=0
    g80: LineSegment StartX=104 StartY=453.38 StartZ=0 EndX=104 EndY=467.88 EndZ=0
    g81: LineSegment StartX=104 StartY=467.88 StartZ=0 EndX=95 EndY=467.88 EndZ=0
    g82: LineSegment StartX=95 StartY=467.88 StartZ=0 EndX=95 EndY=453.38 EndZ=0
    g83: LineSegment StartX=107 StartY=453.38 StartZ=0 EndX=117 EndY=453.38 EndZ=0
    g84: LineSegment StartX=117 StartY=453.38 StartZ=0 EndX=117 EndY=467.88 EndZ=0
    g85: LineSegment StartX=117 StartY=467.88 StartZ=0 EndX=107 EndY=467.88 EndZ=0
    g86: LineSegment StartX=107 StartY=467.88 StartZ=0 EndX=107 EndY=453.38 EndZ=0
  constraints (94):
    c: Coincident(g2,g0)
    c: DistanceY(g0) = 474.93
    c: DistanceX(g0) = 3
    c: DistanceX(g0,g57) = 1
    c: Vertical(g58,g57)
    c: DistanceY(g1) = 471.88
    c: DistanceX(g1) = 28.1
    c: DistanceY(g57,g1) = 4
    c: DistanceY(g58,g1) = 18.5
    c: Coincident(g59,g60)
    c: Coincident(g60,g61)
    c: Coincident(g61,g62)
    c: Coincident(g62,g59)
    c: Horizontal(g59)
    c: Horizontal(g61)
    c: Vertical(g60)
    c: Vertical(g62)
    c: Horizontal(g61,g57)
    c: Horizontal(g59,g58)
    c: DistanceX(g57,g61) = 2.5
    c: DistanceX(g57,g60) = 16.5
    c: Coincident(g63,g64)
    c: Coincident(g64,g65)
    c: Coincident(g65,g66)
    c: Coincident(g66,g63)
    c: Horizontal(g63)
    c: Horizontal(g65)
    c: Vertical(g64)
    c: Vertical(g66)
    c: Horizontal(g65,g60)
    c: Horizontal(g63,g59)
    c: DistanceX(g57,g65) = 19
    c: DistanceX(g57,g64) = 32.5
    c: Coincident(g67,g68)
    c: Coincident(g68,g69)
    c: Coincident(g69,g70)
    c: Coincident(g70,g67)
    c: Horizontal(g67)
    c: Horizontal(g69)
    c: Vertical(g68)
    c: Vertical(g70)
    c: Horizontal(g67,g64)
    c: Horizontal(g69,g63)
    c: DistanceX(g57,g67) = 35
    c: DistanceX(g57,g67) = 49
    c: Coincident(g71,g72)
    c: Coincident(g72,g73)
    c: Coincident(g73,g74)
    c: Coincident(g74,g71)
    c: Horizontal(g71)
    c: Horizontal(g73)
    c: Vertical(g72)
    c: Vertical(g74)
    c: Horizontal(g71,g68)
    c: Horizontal(g73,g67)
    c: DistanceX(g57,g73) = 51
    c: DistanceX(g57,g72) = 64.5
    c: Coincident(g75,g76)
    c: Coincident(g76,g77)
    c: Coincident(g77,g78)
    c: Coincident(g78,g75)
    c: Horizontal(g75)
    c: Horizontal(g77)
    c: Vertical(g76)
    c: Vertical(g78)
    c: Horizontal(g77,g72)
    c: Horizontal(g75,g71)
    c: DistanceX(g57,g77) = 72
    c: DistanceX(g57,g76) = 89
    c: Coincident(g79,g80)
    c: Coincident(g80,g81)
    c: Coincident(g81,g82)
    c: Coincident(g82,g79)
    c: Horizontal(g79)
    c: Horizontal(g81)
    c: Vertical(g80)
    c: Vertical(g82)
    c: Horizontal(g81,g76)
    c: Horizontal(g79,g75)
    c: DistanceX(g57,g81) = 91
    c: DistanceX(g57,g80) = 100
    c: Coincident(g83,g84)
    c: Coincident(g84,g85)
    c: Coincident(g85,g86)
    c: Coincident(g86,g83)
    c: Horizontal(g83)
    c: Horizontal(g85)
    c: Vertical(g84)
    c: Vertical(g86)
    c: Horizontal(g85,g80)
    c: Horizontal(g83,g79)
    c: DistanceX(g57,g85) = 103
    c: DistanceX(g57,g84) = 113
    c: Diameter(g56) = 11
